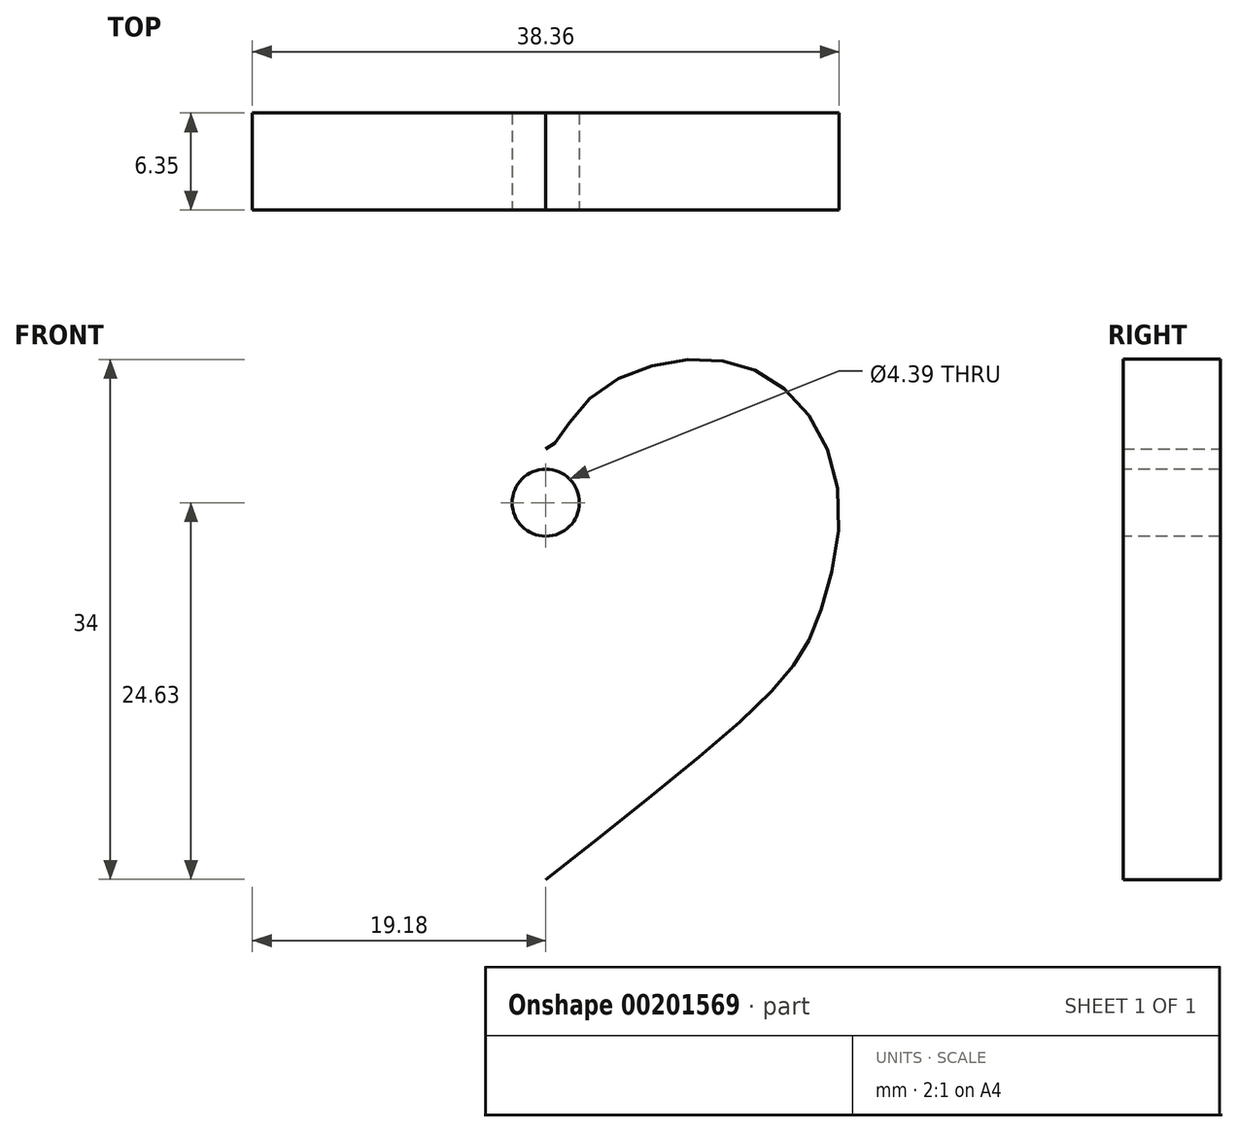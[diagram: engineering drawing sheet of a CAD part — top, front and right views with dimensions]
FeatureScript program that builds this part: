
annotation { "Feature Type Name" : "Feature", "Feature Type Description" : "" }
export const myFeature = defineFeature(function(context is Context, id is Id, definition is map)
    precondition{}
    {
        {
            var Q0;
            Q0=qCreatedBy(makeId("Front.planeOp"),FACE);
            var sketch = newSketch(context, id + "F0", { "sketchPlane" : qUnion([Q0])});
            skFitSpline(sketch, "E0", {"points": [v(37.13, -0.9) * mm, v(51.84, 11.35) * mm, v(54.82, 15.92) * mm, v(56.21, 24.67) * mm, v(52.44, 31.43) * mm, v(46.47, 33.1) * mm, v(40.11, 30.63) * mm, v(37.53, 27.45) * mm, v(37.13, 27.25) * mm, v(37.33, 27.45) * mm], "startDerivative": vector(84.01, 65.85) * mm, "endDerivative": vector(12.17, 10.14) * mm});
            skLineSegment(sketch, "E1", {"start": v(37.13, 27.25) * mm, "end": v(37.13, -0.9) * mm});
            skFitSpline(sketch, "E2.MirrorCS", {"points": [v(37.13, -0.9) * mm, v(22.42, 11.35) * mm, v(19.44, 15.92) * mm, v(18.05, 24.67) * mm, v(21.83, 31.43) * mm, v(27.79, 33.1) * mm, v(34.15, 30.63) * mm, v(36.73, 27.45) * mm, v(37.13, 27.25) * mm, v(36.93, 27.45) * mm], "startDerivative": vector(-84.01, 65.85) * mm, "endDerivative": vector(-12.17, 10.14) * mm});
            skSolve(sketch);
        }
        {
            var Q0;
            Q0 = qSketchRegion(id + "F0", true);
            extrude(context, id + "F1", {"entities" : qUnion([Q0]), "depth" : 6.35 * mm});
        }
        {
            var Q0;
            {var subQ0=sQuery(id+"F0.wireOp",EDGE,"E2.MirrorCS");var subQ1=sQuery(id+"F0.wireOp",EDGE,"E1");var subQ2=sQuery(id+"F0.wireOp",EDGE,"E0");var subQ3=makeQuery(id+"F0.imprint","INTERSECT",VERTEX,{"disambiguationData":[OD(0.0)],"derivedFrom":[subQ2,subQ1,subQ0]});Q0=makeQuery(id+"F1.opExtrude","CAP_FACE",FACE,{"disambiguationData":[OSD([subQ2,subQ0]),TDD([makeQuery(id+"F0.imprint","IMPRINT",EDGE,{"disambiguationData":[TD([[subQ3,-1.0]])],"derivedFrom":subQ2}),makeQuery(id+"F0.imprint","IMPRINT",EDGE,{"disambiguationData":[TD([[subQ3,-1.0]])],"derivedFrom":subQ0})])],"isStart":false});}
            var sketch = newSketch(context, id + "F2", { "sketchPlane" : qUnion([Q0])});
            skCircle(sketch, "E3", {"center": v(37.13, 23.74) * mm, "radius": 2.2 * mm});
            skSolve(sketch);
        }
        {
            var Q0;
            Q0 = qSketchRegion(id + "F2", true);
            extrude(context, id + "F3", {"entities" : qUnion([Q0]), "operationType" : NewBodyOperationType.REMOVE, "oppositeDirection" : true, "depth" : 25.4 * mm});
        }
    });
